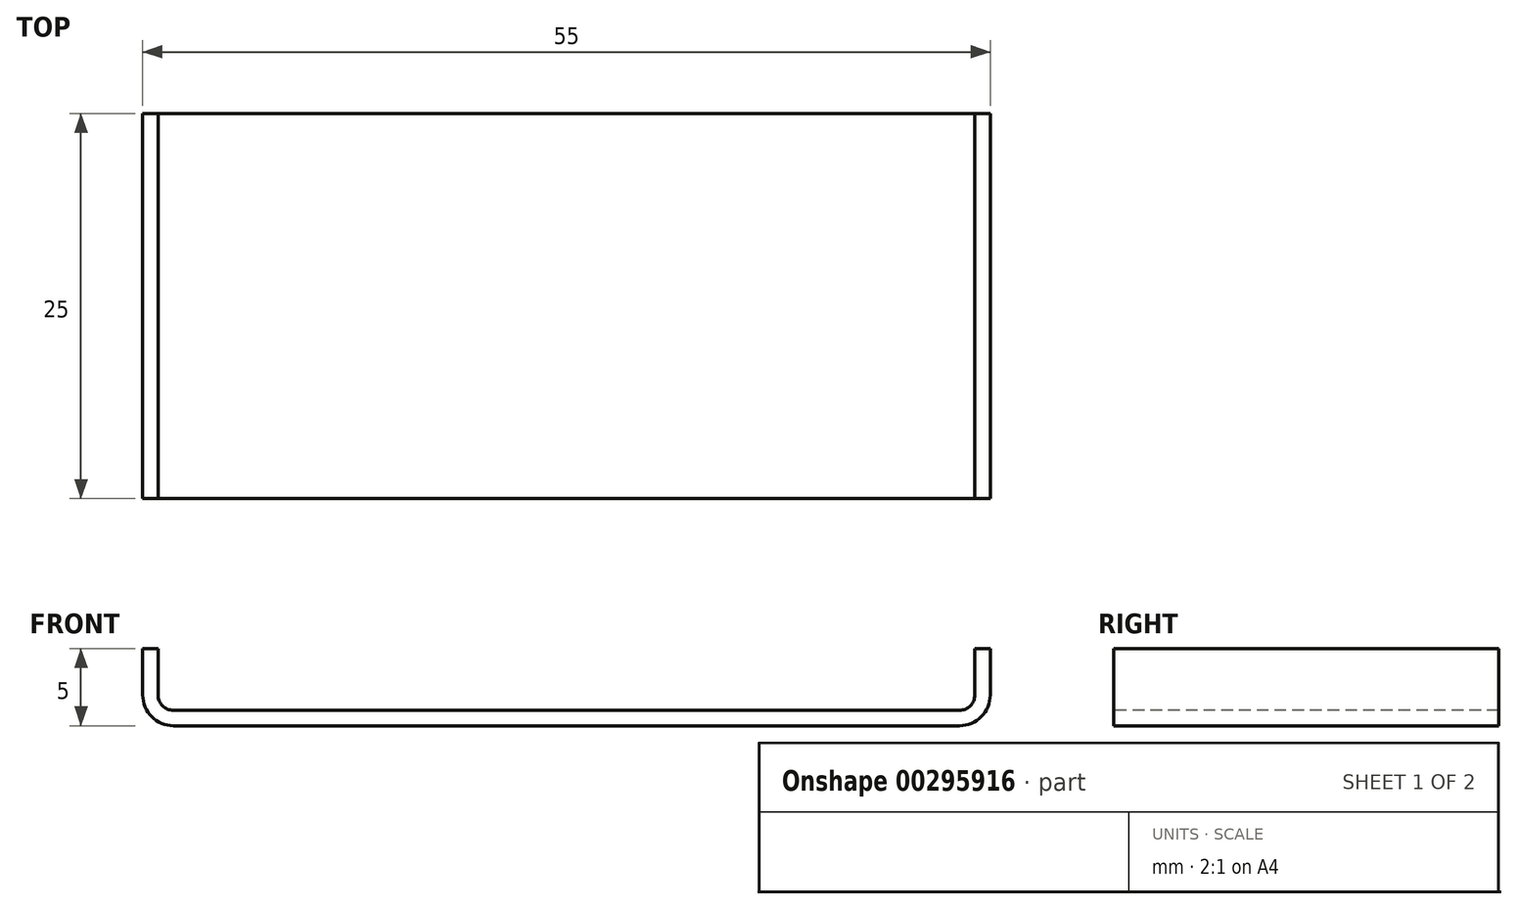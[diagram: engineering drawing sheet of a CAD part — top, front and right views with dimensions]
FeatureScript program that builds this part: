
annotation { "Feature Type Name" : "Feature", "Feature Type Description" : "" }
export const myFeature = defineFeature(function(context is Context, id is Id, definition is map)
    precondition{}
    {
        {
            var Q0;
            Q0=qCreatedBy(makeId("Front.planeOp"),FACE);
            var sketch = newSketch(context, id + "F0", { "sketchPlane" : qUnion([Q0])});
            skLineSegment(sketch, "E0", {"start": v(-27.5, 5) * mm, "end": v(-27.5, 2) * mm});
            skLineSegment(sketch, "E1", {"start": v(-25.5, 0) * mm, "end": v(25.5, 0) * mm});
            skLineSegment(sketch, "E2", {"start": v(27.5, 2) * mm, "end": v(27.5, 5) * mm});
            skPoint(sketch, "E3.visualSharp", {"position": v(-27.5, 0) * mm});
            skArc(sketch, "E3.filletArc", {"start": v(-27.5, 2) * mm, "mid": v(-26.91, 0.59) * mm, "end": v(-25.5, 0) * mm});
            skPoint(sketch, "E4.visualSharp", {"position": v(27.5, 0) * mm});
            skArc(sketch, "E4.filletArc", {"start": v(25.5, 0) * mm, "mid": v(26.91, 0.59) * mm, "end": v(27.5, 2) * mm});
            skLineSegment(sketch, "E5.0", {"start": v(26.5, 2) * mm, "end": v(26.5, 5) * mm});
            skLineSegment(sketch, "E5.1", {"start": v(-25.5, 1) * mm, "end": v(25.5, 1) * mm});
            skLineSegment(sketch, "E5.2", {"start": v(-26.5, 5) * mm, "end": v(-26.5, 2) * mm});
            skPoint(sketch, "E6.visualSharp", {"position": v(-26.5, 1) * mm});
            skArc(sketch, "E6.filletArc", {"start": v(-26.5, 2) * mm, "mid": v(-26.2, 1.3) * mm, "end": v(-25.5, 1) * mm});
            skPoint(sketch, "E7.visualSharp", {"position": v(26.5, 1) * mm});
            skArc(sketch, "E7.filletArc", {"start": v(25.5, 1) * mm, "mid": v(26.2, 1.3) * mm, "end": v(26.5, 2) * mm});
            skLineSegment(sketch, "E8", {"start": v(-26.5, 5) * mm, "end": v(-27.5, 5) * mm});
            skLineSegment(sketch, "E9", {"start": v(26.5, 5) * mm, "end": v(27.5, 5) * mm});
            skSolve(sketch);
        }
        {
            var Q0;
            Q0 = qSketchRegion(id + "F0", true);
            extrude(context, id + "F1", {"entities" : qUnion([Q0]), "oppositeDirection" : true, "depth" : 25 * mm});
        }
    });
